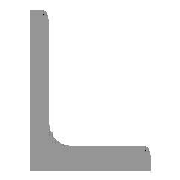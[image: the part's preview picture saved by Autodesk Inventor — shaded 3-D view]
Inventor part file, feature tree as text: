
AUTODESK INVENTOR PART (.ipt)
format: ipt  version: 2022 (Build 260153000, 153)  size: 247,808 bytes
history: native  units: mm (DEFAULTED — no unit token found)
features: other x7, sketch x3, surface_op x2, plane x1
ambient origin geometry x8: Origin, YZ Plane, XZ Plane, XY Plane, X Axis, Y Axis, Z Axis, Center Point
bodies: Solid1 (feature_tree), Body (feature_tree), Solid3 (feature_tree)
feature tree (13):
  parser-record x1  (decoder bookkeeping rows leaked as tree rows — omitted from the tree; the rows remain in map.json)
  other  "Driven Length"
  other  "Start Plane"
  other  "End Plane"
  sketch  "Sketch"  dims[d5=50.0mm d6=30.0mm d7=4.0mm d8=3.0mm d9=4.0mm d10=3.0mm d11=140.857864mm d12=0.0mm d17=5.0mm d18=2.5mm d19=8.3mm d20=8.3mm d21=-0.0mm d22=180.0mm d23=90.0deg d24=180.0mm d43=5.0mm d44=5.0mm d45=5.0mm d46=5.0mm d47=5.0mm d48=5.0mm d49=5.0mm d50=5.0mm d51=0.0mm d52=5.0mm d53=5.0mm d54=5.0mm d55=5.0mm d56=5.0mm d57=5.0mm d58=5.0mm d59=5.0mm d60=0.0mm]
  sketch  "Sketch3"  dims[d3=50.0mm]
  plane  "Work Plane10"
  sketch  "Sketch4"  dims[d4=30.0mm]
  other  "Srf5"
  other  "Srf6"
  other  "Srf4"
  surface_op  "Boundary Patch3"
  surface_op  "Boundary Patch4"
